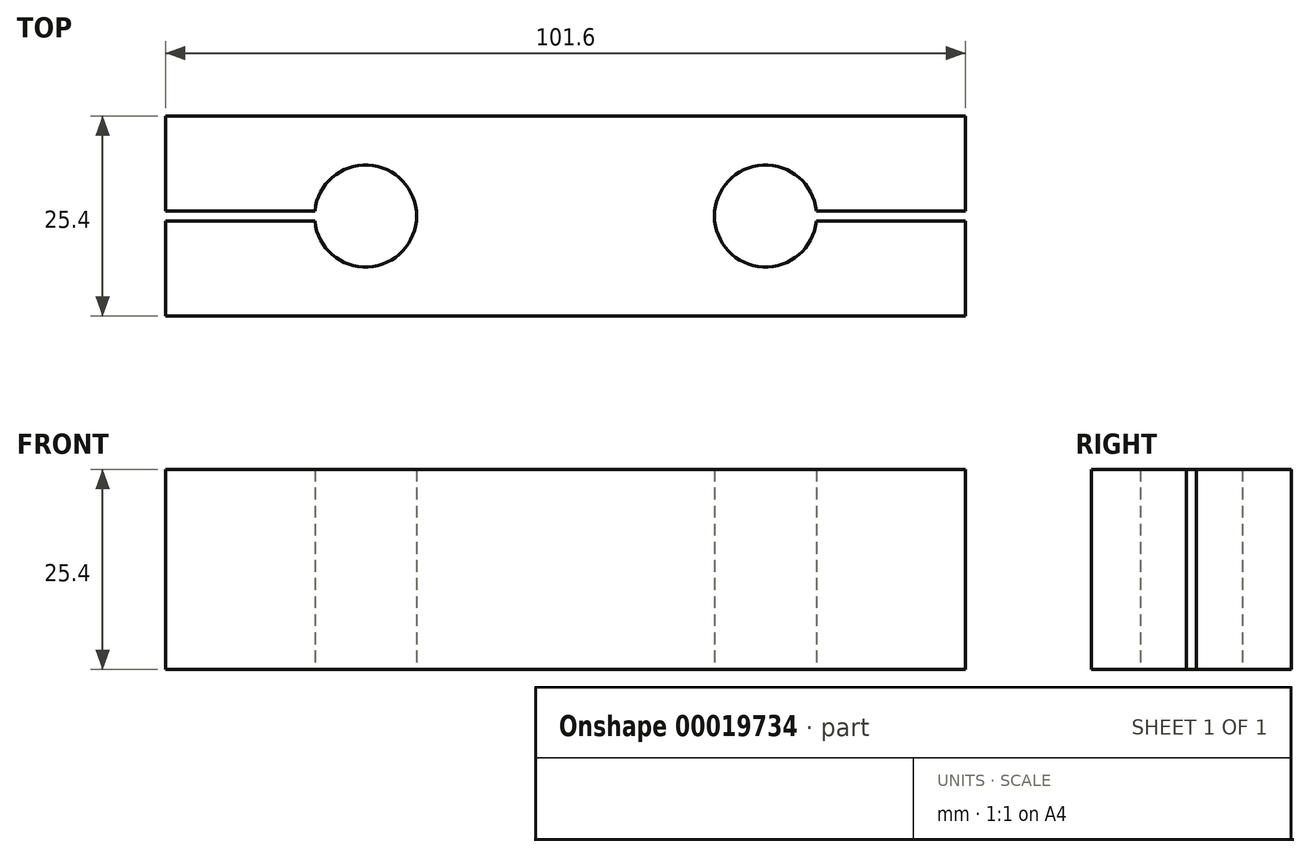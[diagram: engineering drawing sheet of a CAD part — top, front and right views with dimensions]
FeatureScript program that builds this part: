
annotation { "Feature Type Name" : "Feature", "Feature Type Description" : "" }
export const myFeature = defineFeature(function(context is Context, id is Id, definition is map)
    precondition{}
    {
        {
            var Q0;
            Q0=qCreatedBy(makeId("Top.planeOp"),FACE);
            var sketch = newSketch(context, id + "F0", { "sketchPlane" : qUnion([Q0])});
            skLineSegment(sketch, "E0.bottom", {"start": v(0, 0) * mm, "end": v(101.6, 0) * mm});
            skLineSegment(sketch, "E0.top", {"start": v(0, 25.4) * mm, "end": v(101.6, 25.4) * mm});
            skLineSegment(sketch, "E0.left", {"start": v(0, 0) * mm, "end": v(0, 12.07) * mm});
            skLineSegment(sketch, "E0.right", {"start": v(101.6, 0) * mm, "end": v(101.6, 12.07) * mm});
            skLineSegment(sketch, "E1", {"start": v(0, 12.7) * mm, "end": v(101.6, 12.7) * mm, "construction": true});
            skLineSegment(sketch, "E2", {"start": v(50.8, 25.4) * mm, "end": v(50.8, 0) * mm, "construction": true});
            skLineSegment(sketch, "E3", {"start": v(25.4, 25.4) * mm, "end": v(25.4, 0) * mm, "construction": true});
            skLineSegment(sketch, "E4.MirrorCS", {"start": v(76.2, 25.4) * mm, "end": v(76.2, 0) * mm, "construction": true});
            skArc(sketch, "E5", {"start": v(18.95, 12.07) * mm, "mid": v(31.88, 12.7) * mm, "end": v(18.95, 13.34) * mm});
            skArc(sketch, "E6", {"start": v(82.65, 13.34) * mm, "mid": v(69.72, 12.7) * mm, "end": v(82.65, 12.07) * mm});
            skLineSegment(sketch, "E7", {"start": v(0, 13.34) * mm, "end": v(18.95, 13.34) * mm});
            skLineSegment(sketch, "E8", {"start": v(18.95, 12.07) * mm, "end": v(0, 12.07) * mm});
            skLineSegment(sketch, "E9", {"start": v(82.65, 13.34) * mm, "end": v(101.6, 13.34) * mm});
            skLineSegment(sketch, "E10", {"start": v(101.6, 12.07) * mm, "end": v(82.65, 12.07) * mm});
            skLineSegment(sketch, "E11.trimOffspring", {"start": v(0, 13.34) * mm, "end": v(0, 25.4) * mm});
            skLineSegment(sketch, "E12.trimOffspring", {"start": v(101.6, 13.34) * mm, "end": v(101.6, 25.4) * mm});
            skSolve(sketch);
        }
        {
            var Q0;
            Q0=makeQuery(id+"F0.imprint","IMPRINT",FACE,{"disambiguationData":[TD([[makeQuery(id+"F0.imprint","IMPRINT",EDGE,{"derivedFrom":sQuery(id+"F0.wireOp",EDGE,"E0.bottom")}),1.0]])]});
            extrude(context, id + "F1", {"entities" : qUnion([Q0]), "depth" : 25.4 * mm});
        }
    });
